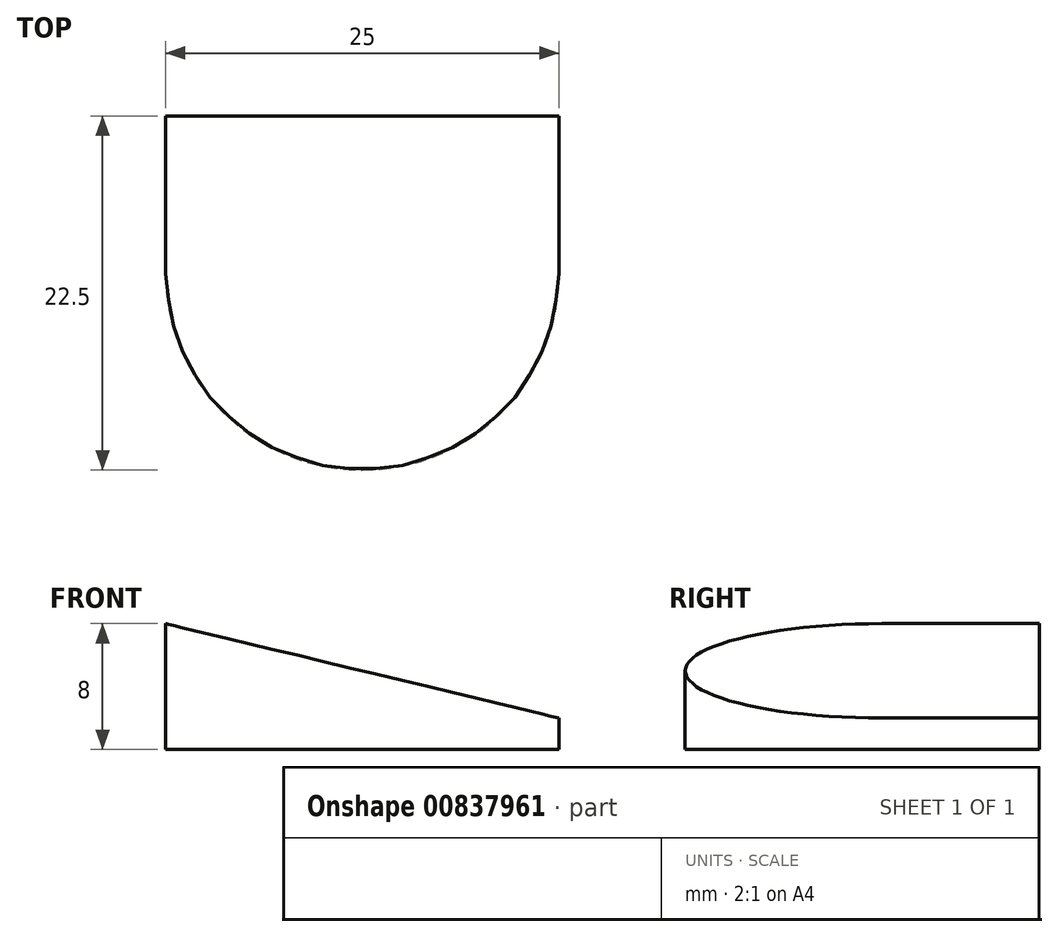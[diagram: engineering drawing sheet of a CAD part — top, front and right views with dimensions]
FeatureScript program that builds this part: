
annotation { "Feature Type Name" : "Feature", "Feature Type Description" : "" }
export const myFeature = defineFeature(function(context is Context, id is Id, definition is map)
    precondition{}
    {
        {
            var Q0;
            Q0=qCreatedBy(makeId("Top.planeOp"),FACE);
            var sketch = newSketch(context, id + "F0", { "sketchPlane" : qUnion([Q0])});
            skLineSegment(sketch, "E0", {"start": v(0, 0) * mm, "end": v(0, 10) * mm});
            skLineSegment(sketch, "E1", {"start": v(0, 10) * mm, "end": v(25, 10) * mm});
            skLineSegment(sketch, "E2", {"start": v(25, 10) * mm, "end": v(25, 0) * mm});
            skArc(sketch, "E3", {"start": v(0, 0) * mm, "mid": v(12.5, -12.5) * mm, "end": v(25, 0) * mm});
            skSolve(sketch);
        }
        {
            var Q0;
            Q0 = qSketchRegion(id + "F0", true);
            extrude(context, id + "F1", {"entities" : qUnion([Q0]), "depth" : 25 * mm, "offsetDistance" : 25 * mm});
        }
        {
            var Q0;
            Q0=qCreatedBy(makeId("Front.planeOp"),FACE);
            var sketch = newSketch(context, id + "F2", { "sketchPlane" : qUnion([Q0])});
            skLineSegment(sketch, "E4", {"start": v(-8.59, 10.06) * mm, "end": v(30.77, 0.61) * mm});
            skLineSegment(sketch, "E5", {"start": v(30.77, 0.61) * mm, "end": v(30.77, 30.9) * mm});
            skLineSegment(sketch, "E6", {"start": v(30.77, 30.9) * mm, "end": v(-8.59, 40.34) * mm});
            skLineSegment(sketch, "E7", {"start": v(-8.59, 40.34) * mm, "end": v(-8.59, 10.06) * mm});
            skPoint(sketch, "E8", {"position": v(25, 2) * mm});
            skPoint(sketch, "E9", {"position": v(0, 8) * mm});
            skSolve(sketch);
        }
        {
            var Q0;
            Q0 = qSketchRegion(id + "F2", true);
            extrude(context, id + "F3", {"entities" : qUnion([Q0]), "operationType" : NewBodyOperationType.REMOVE, "endBound" : BoundingType.SYMMETRIC, "depth" : 60 * mm, "offsetDistance" : 25 * mm});
        }
    });
